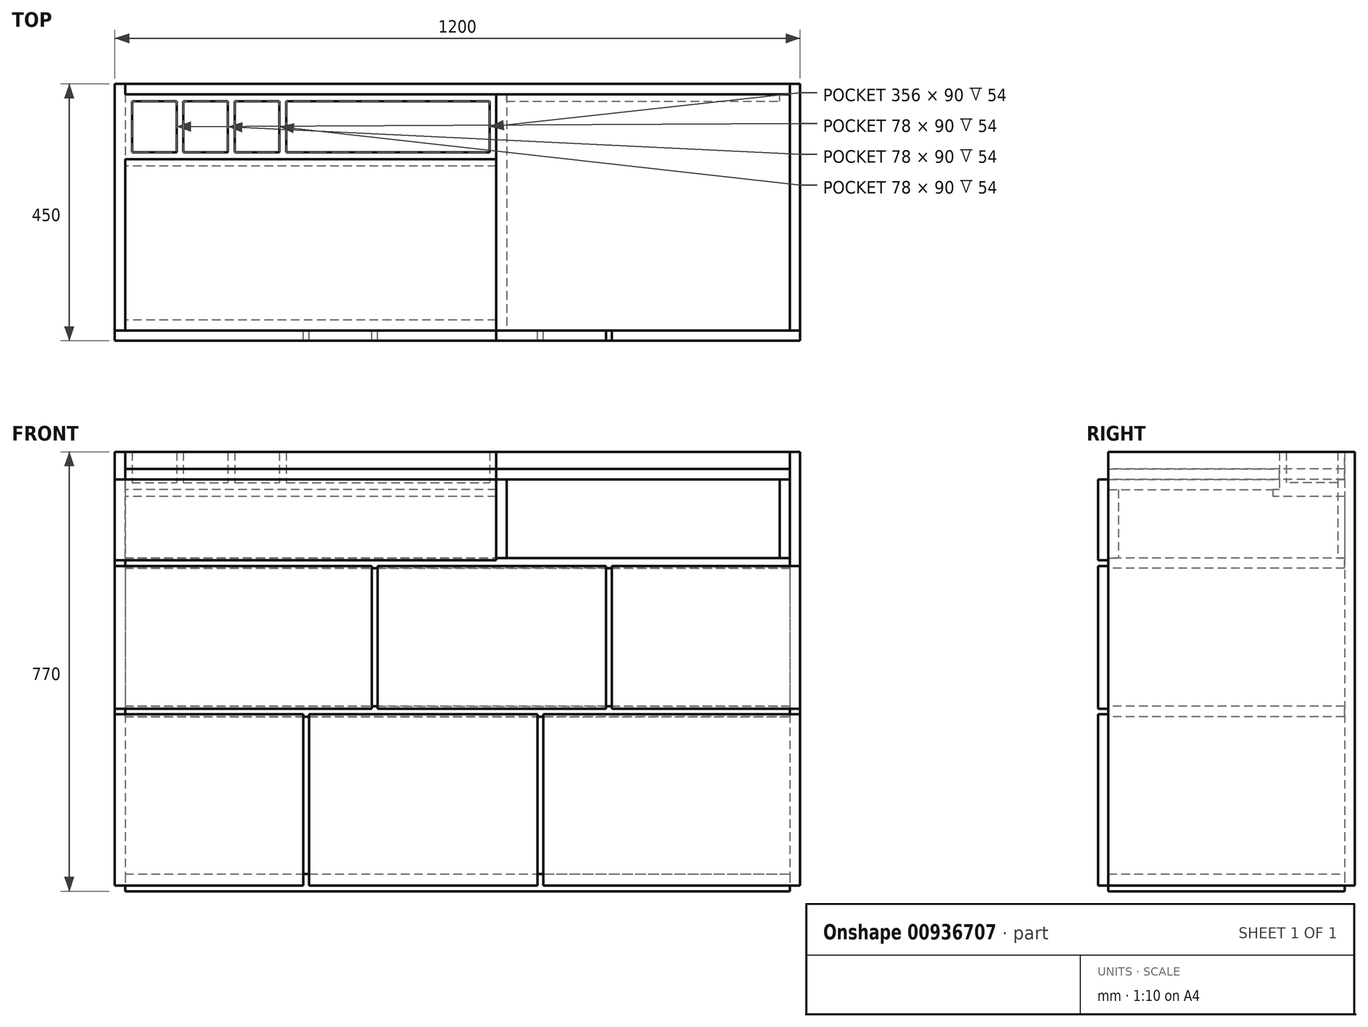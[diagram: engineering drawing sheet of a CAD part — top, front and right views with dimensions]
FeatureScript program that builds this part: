
annotation { "Feature Type Name" : "Feature", "Feature Type Description" : "" }
export const myFeature = defineFeature(function(context is Context, id is Id, definition is map)
    precondition{}
    {
        {
            var Q0;
            Q0=qCreatedBy(makeId("Top.planeOp"),FACE);
            var sketch = newSketch(context, id + "F0", { "sketchPlane" : qUnion([Q0])});
            skLineSegment(sketch, "E0.bottom", {"start": v(0, 0) * mm, "end": v(1200, 0) * mm});
            skLineSegment(sketch, "E0.top", {"start": v(0, 432) * mm, "end": v(1200, 432) * mm});
            skLineSegment(sketch, "E0.left", {"start": v(0, 0) * mm, "end": v(0, 432) * mm});
            skLineSegment(sketch, "E0.right", {"start": v(1200, 0) * mm, "end": v(1200, 432) * mm});
            skLineSegment(sketch, "E1.0", {"start": v(18, 0) * mm, "end": v(18, 432) * mm});
            skLineSegment(sketch, "E2", {"start": v(600, 455.77) * mm, "end": v(600, 504.04) * mm, "construction": true});
            skPoint(sketch, "E2.startSnap0", {"position": v(600, 432) * mm});
            skLineSegment(sketch, "E3.MirrorCS", {"start": v(1182, 0) * mm, "end": v(1182, 432) * mm});
            skLineSegment(sketch, "E4", {"start": v(1225.2, 216) * mm, "end": v(1296.23, 216) * mm, "construction": true});
            skPoint(sketch, "E4.startSnap0", {"position": v(1200, 216) * mm});
            skLineSegment(sketch, "E5.0", {"start": v(0, 414) * mm, "end": v(1200, 414) * mm});
            skSolve(sketch);
        }
        {
            var Q0;
            {var subQ0=sQuery(id+"F0.wireOp",EDGE,"E0.left");var subQ1=sQuery(id+"F0.wireOp",EDGE,"E0.bottom");var subQ2=makeQuery(id+"F0.imprint","INTERSECT",VERTEX,{"derivedFrom":[subQ1,subQ0]});Q0=makeQuery(id+"F0.imprint","IMPRINT",FACE,{"disambiguationData":[TD([[makeQuery(id+"F0.imprint","IMPRINT",EDGE,{"disambiguationData":[TD([[subQ2,-1.0]])],"derivedFrom":subQ1}),1.0]])]});}
            var Q1;
            {var subQ0=sQuery(id+"F0.wireOp",EDGE,"E0.left");var subQ1=sQuery(id+"F0.wireOp",EDGE,"E0.top");var subQ2=makeQuery(id+"F0.imprint","INTERSECT",VERTEX,{"derivedFrom":[subQ1,subQ0]});Q1=makeQuery(id+"F0.imprint","IMPRINT",FACE,{"disambiguationData":[TD([[makeQuery(id+"F0.imprint","IMPRINT",EDGE,{"disambiguationData":[TD([[subQ2,-1.0]])],"derivedFrom":subQ1}),-1.0]])]});}
            var Q2;
            {var subQ0=sQuery(id+"F0.wireOp",EDGE,"E0.right");var subQ1=sQuery(id+"F0.wireOp",EDGE,"E0.bottom");var subQ2=makeQuery(id+"F0.imprint","INTERSECT",VERTEX,{"derivedFrom":[subQ1,subQ0]});Q2=makeQuery(id+"F0.imprint","IMPRINT",FACE,{"disambiguationData":[TD([[makeQuery(id+"F0.imprint","IMPRINT",EDGE,{"disambiguationData":[TD([[subQ2,1.0]])],"derivedFrom":subQ1}),1.0]])]});}
            var Q3;
            {var subQ0=sQuery(id+"F0.wireOp",EDGE,"E0.right");var subQ1=sQuery(id+"F0.wireOp",EDGE,"E0.top");var subQ2=makeQuery(id+"F0.imprint","INTERSECT",VERTEX,{"derivedFrom":[subQ1,subQ0]});Q3=makeQuery(id+"F0.imprint","IMPRINT",FACE,{"disambiguationData":[TD([[makeQuery(id+"F0.imprint","IMPRINT",EDGE,{"disambiguationData":[TD([[subQ2,1.0]])],"derivedFrom":subQ1}),-1.0]])]});}
            extrude(context, id + "F1", {"entities" : qUnion([Q0, Q1, Q2, Q3]), "depth" : 760 * mm, "offsetDistance" : 25 * mm});
        }
        {
            var Q0;
            {var subQ0=sQuery(id+"F0.wireOp",EDGE,"E1.0");var subQ1=sQuery(id+"F0.wireOp",EDGE,"E0.top");var subQ2=makeQuery(id+"F0.imprint","INTERSECT",VERTEX,{"derivedFrom":[subQ1,subQ0]});Q0=makeQuery(id+"F0.imprint","IMPRINT",FACE,{"disambiguationData":[TD([[makeQuery(id+"F0.imprint","IMPRINT",EDGE,{"disambiguationData":[TD([[subQ2,-1.0]])],"derivedFrom":subQ1}),-1.0]])]});}
            var Q1;
            Q1=makeQuery(id+"F1.opExtrude","CAP_FACE",FACE,{"disambiguationData":[OSD([sQuery(id+"F0.wireOp",EDGE,"E0.bottom"),sQuery(id+"F0.wireOp",EDGE,"E0.top"),sQuery(id+"F0.wireOp",EDGE,"E0.left"),sQuery(id+"F0.wireOp",EDGE,"E1.0")])],"isStart":false});
            extrude(context, id + "F2", {"entities" : qUnion([Q0]), "endBound" : BoundingType.UP_TO_SURFACE, "depth" : 25 * mm, "endBoundEntityFace" : qUnion([Q1]), "offsetDistance" : 25 * mm});
        }
        {
            var Q0;
            {var subQ0=sQuery(id+"F0.wireOp",EDGE,"E1.0");var subQ1=sQuery(id+"F0.wireOp",EDGE,"E0.bottom");var subQ2=makeQuery(id+"F0.imprint","INTERSECT",VERTEX,{"derivedFrom":[subQ1,subQ0]});Q0=makeQuery(id+"F0.imprint","IMPRINT",FACE,{"disambiguationData":[TD([[makeQuery(id+"F0.imprint","IMPRINT",EDGE,{"disambiguationData":[TD([[subQ2,-1.0]])],"derivedFrom":subQ1}),1.0]])]});}
            extrude(context, id + "F3", {"entities" : qUnion([Q0]), "depth" : 20 * mm, "offsetDistance" : 25 * mm, "hasSecondDirection" : true, "secondDirectionOppositeDirection" : true, "secondDirectionDepth" : 10 * mm});
        }
        {
            var Q0;
            Q0=makeQuery(id+"F1.opExtrude","CAP_FACE",FACE,{"disambiguationData":[OSD([sQuery(id+"F0.wireOp",EDGE,"E0.bottom"),sQuery(id+"F0.wireOp",EDGE,"E0.top"),sQuery(id+"F0.wireOp",EDGE,"E0.left"),sQuery(id+"F0.wireOp",EDGE,"E1.0")])],"isStart":false});
            var sketch = newSketch(context, id + "F4", { "sketchPlane" : qUnion([Q0])});
            skLineSegment(sketch, "E6.bottom", {"start": v(0, 432) * mm, "end": v(1200, 432) * mm});
            skLineSegment(sketch, "E6.top", {"start": v(0, 0) * mm, "end": v(1200, 0) * mm});
            skLineSegment(sketch, "E6.left", {"start": v(0, 432) * mm, "end": v(0, 0) * mm});
            skLineSegment(sketch, "E6.right", {"start": v(1200, 432) * mm, "end": v(1200, 0) * mm});
            skLineSegment(sketch, "E7.bottom", {"start": v(18, 0) * mm, "end": v(1182, 0) * mm});
            skLineSegment(sketch, "E7.top", {"start": v(18, 414) * mm, "end": v(1182, 414) * mm});
            skLineSegment(sketch, "E7.left", {"start": v(18, 0) * mm, "end": v(18, 414) * mm});
            skLineSegment(sketch, "E7.right", {"start": v(1182, 0) * mm, "end": v(1182, 414) * mm});
            skLineSegment(sketch, "E8", {"start": v(668, 414) * mm, "end": v(668, 0) * mm});
            skLineSegment(sketch, "E9", {"start": v(18, 300) * mm, "end": v(668, 300) * mm});
            skLineSegment(sketch, "E10", {"start": v(55.2, 414) * mm, "end": v(55.2, -186) * mm, "construction": true});
            skLineSegment(sketch, "E11", {"start": v(-81.86, 114) * mm, "end": v(55.2, 114) * mm, "construction": true});
            skLineSegment(sketch, "E12", {"start": v(55.2, 0) * mm, "end": v(-78.13, 0) * mm, "construction": true});
            skLineSegment(sketch, "E13", {"start": v(55.2, -186) * mm, "end": v(-68.9, -186) * mm, "construction": true});
            skSolve(sketch);
        }
        {
            var Q0;
            {var subQ5=sQuery(id+"F4.wireOp",EDGE,"E9");Q0=makeQuery(id+"F4.imprint","IMPRINT",FACE,{"disambiguationData":[TD([[makeQuery(id+"F4.imprint","IMPRINT",EDGE,{"derivedFrom":subQ5}),-1.0]])]});}
            extrude(context, id + "F5", {"entities" : qUnion([Q0]), "oppositeDirection" : true, "depth" : 18 * mm, "offsetDistance" : 25 * mm});
        }
        {
            var Q0;
            {var subQ0=sQuery(id+"F4.wireOp",EDGE,"E7.right");Q0=makeQuery(id+"F4.imprint","IMPRINT",FACE,{"disambiguationData":[TD([[makeQuery(id+"F4.imprint","IMPRINT",EDGE,{"derivedFrom":subQ0}),1.0]])]});}
            extrude(context, id + "F6", {"entities" : qUnion([Q0]), "oppositeDirection" : true, "depth" : 18 * mm, "offsetDistance" : 25 * mm});
        }
        {
            var Q0;
            Q0=makeQuery(id+"F5.opExtrude","SWEPT_BODY",BODY,{"disambiguationData":[OSD([sQuery(id+"F4.wireOp",EDGE,"E7.bottom"),sQuery(id+"F4.wireOp",EDGE,"E7.top"),sQuery(id+"F4.wireOp",EDGE,"E7.left"),sQuery(id+"F4.wireOp",EDGE,"E8")])]});
            var Q1;
            Q1=makeQuery(id+"F6.opExtrude","SWEPT_BODY",BODY,{"disambiguationData":[OSD([sQuery(id+"F4.wireOp",EDGE,"E7.bottom"),sQuery(id+"F4.wireOp",EDGE,"E7.top"),sQuery(id+"F4.wireOp",EDGE,"E7.right"),sQuery(id+"F4.wireOp",EDGE,"E8")])]});
            transform(context, id + "F7", {"entities" : qUnion([Q0, Q1]), "transformType" : TransformType.TRANSLATION_3D, "dx" : 0 * mm, "dy" : 0 * mm, "dz" : -30 * mm, "makeCopy" : false});
        }
        {
            var Q0;
            {var subQ0=sQuery(id+"F0.wireOp",EDGE,"E0.bottom");Q0=makeQuery(id+"F1.opExtrude","SWEPT_FACE",FACE,{"disambiguationData":[OSD([subQ0]),TDD([makeQuery(id+"F0.imprint","IMPRINT",EDGE,{"disambiguationData":[TD([[makeQuery(id+"F0.imprint","INTERSECT",VERTEX,{"derivedFrom":[subQ0,sQuery(id+"F0.wireOp",EDGE,"E0.left")]}),-1.0]])],"derivedFrom":subQ0})])]});}
            var sketch = newSketch(context, id + "F8", { "sketchPlane" : qUnion([Q0])});
            skLineSegment(sketch, "E14.bottom", {"start": v(0, 730) * mm, "end": v(668, 730) * mm});
            skLineSegment(sketch, "E14.top", {"start": v(0, 570) * mm, "end": v(668, 570) * mm});
            skLineSegment(sketch, "E14.left", {"start": v(0, 730) * mm, "end": v(0, 570) * mm});
            skLineSegment(sketch, "E14.right", {"start": v(668, 730) * mm, "end": v(668, 570) * mm});
            skLineSegment(sketch, "E15.bottom", {"start": v(1200, 560) * mm, "end": v(870, 560) * mm});
            skLineSegment(sketch, "E15.top", {"start": v(1200, 310) * mm, "end": v(870, 310) * mm});
            skLineSegment(sketch, "E15.left", {"start": v(1200, 560) * mm, "end": v(1200, 310) * mm});
            skLineSegment(sketch, "E15.right", {"start": v(870, 560) * mm, "end": v(870, 310) * mm});
            skLineSegment(sketch, "E16.bottom", {"start": v(860, 560) * mm, "end": v(460, 560) * mm});
            skLineSegment(sketch, "E16.top", {"start": v(860, 310) * mm, "end": v(460, 310) * mm});
            skLineSegment(sketch, "E16.left", {"start": v(860, 560) * mm, "end": v(860, 310) * mm});
            skLineSegment(sketch, "E16.right", {"start": v(460, 560) * mm, "end": v(460, 310) * mm});
            skLineSegment(sketch, "E17.bottom", {"start": v(450, 560) * mm, "end": v(0, 560) * mm});
            skLineSegment(sketch, "E17.top", {"start": v(450, 310) * mm, "end": v(0, 310) * mm});
            skLineSegment(sketch, "E17.left", {"start": v(450, 560) * mm, "end": v(450, 310) * mm});
            skLineSegment(sketch, "E17.right", {"start": v(0, 560) * mm, "end": v(0, 310) * mm});
            skLineSegment(sketch, "E18.bottom", {"start": v(678, 730) * mm, "end": v(1200, 730) * mm});
            skLineSegment(sketch, "E18.top", {"start": v(678, 570) * mm, "end": v(1200, 570) * mm});
            skLineSegment(sketch, "E18.left", {"start": v(678, 730) * mm, "end": v(678, 570) * mm});
            skLineSegment(sketch, "E18.right", {"start": v(1200, 730) * mm, "end": v(1200, 570) * mm});
            skLineSegment(sketch, "E19", {"start": v(668, 650) * mm, "end": v(678, 650) * mm, "construction": true});
            skLineSegment(sketch, "E20", {"start": v(1108.22, 570) * mm, "end": v(1108.22, 560) * mm, "construction": true});
            skLineSegment(sketch, "E21", {"start": v(870, 435) * mm, "end": v(860, 435) * mm, "construction": true});
            skLineSegment(sketch, "E22", {"start": v(460, 435) * mm, "end": v(450, 435) * mm, "construction": true});
            skLineSegment(sketch, "E23.bottom", {"start": v(0, 0) * mm, "end": v(330, 0) * mm});
            skLineSegment(sketch, "E23.top", {"start": v(0, 300) * mm, "end": v(330, 300) * mm});
            skLineSegment(sketch, "E23.left", {"start": v(0, 0) * mm, "end": v(0, 300) * mm});
            skLineSegment(sketch, "E23.right", {"start": v(330, 0) * mm, "end": v(330, 300) * mm});
            skLineSegment(sketch, "E24.bottom", {"start": v(340, 300) * mm, "end": v(740, 300) * mm});
            skLineSegment(sketch, "E24.top", {"start": v(340, 0) * mm, "end": v(740, 0) * mm});
            skLineSegment(sketch, "E24.left", {"start": v(340, 300) * mm, "end": v(340, 0) * mm});
            skLineSegment(sketch, "E24.right", {"start": v(740, 300) * mm, "end": v(740, 0) * mm});
            skLineSegment(sketch, "E25.bottom", {"start": v(750, 300) * mm, "end": v(1200, 300) * mm});
            skLineSegment(sketch, "E25.top", {"start": v(750, 0) * mm, "end": v(1200, 0) * mm});
            skLineSegment(sketch, "E25.left", {"start": v(750, 300) * mm, "end": v(750, 0) * mm});
            skLineSegment(sketch, "E25.right", {"start": v(1200, 300) * mm, "end": v(1200, 0) * mm});
            skLineSegment(sketch, "E26", {"start": v(165, 310) * mm, "end": v(165, 300) * mm, "construction": true});
            skPoint(sketch, "E26.startSnap0", {"position": v(165, 300) * mm});
            skLineSegment(sketch, "E27", {"start": v(330, 150) * mm, "end": v(340, 150) * mm, "construction": true});
            skLineSegment(sketch, "E28", {"start": v(750, 150) * mm, "end": v(740, 150) * mm, "construction": true});
            skLineSegment(sketch, "E29.bottom", {"start": v(678, 570) * mm, "end": v(1182, 570) * mm});
            skLineSegment(sketch, "E29.top", {"start": v(678, 588) * mm, "end": v(1182, 588) * mm});
            skLineSegment(sketch, "E29.left", {"start": v(678, 570) * mm, "end": v(678, 588) * mm});
            skLineSegment(sketch, "E29.right", {"start": v(1182, 570) * mm, "end": v(1182, 588) * mm});
            skLineSegment(sketch, "E30", {"start": v(668, 712) * mm, "end": v(0, 712) * mm});
            skSolve(sketch);
        }
        {
            var Q0;
            {var subQ0=sQuery(id+"F8.wireOp",EDGE,"E17.left");Q0=makeQuery(id+"F8.imprint","IMPRINT",FACE,{"disambiguationData":[TD([[makeQuery(id+"F8.imprint","IMPRINT",EDGE,{"derivedFrom":subQ0}),-1.0]])]});}
            var Q1;
            Q1=makeQuery(id+"F8.imprint","IMPRINT",FACE,{"disambiguationData":[TD([[makeQuery(id+"F8.imprint","IMPRINT",EDGE,{"derivedFrom":sQuery(id+"F8.wireOp",EDGE,"E16.bottom")}),1.0]])]});
            var Q2;
            Q2=makeQuery(id+"F8.imprint","IMPRINT",FACE,{"disambiguationData":[TD([[makeQuery(id+"F8.imprint","IMPRINT",EDGE,{"derivedFrom":sQuery(id+"F8.wireOp",EDGE,"E15.bottom")}),1.0]])]});
            var Q3;
            Q3=makeQuery(id+"F8.imprint","IMPRINT",FACE,{"disambiguationData":[TD([[makeQuery(id+"F8.imprint","IMPRINT",EDGE,{"derivedFrom":sQuery(id+"F8.wireOp",EDGE,"E25.bottom")}),-1.0]])]});
            var Q4;
            Q4=makeQuery(id+"F8.imprint","IMPRINT",FACE,{"disambiguationData":[TD([[makeQuery(id+"F8.imprint","IMPRINT",EDGE,{"derivedFrom":sQuery(id+"F8.wireOp",EDGE,"E24.bottom")}),-1.0]])]});
            var Q5;
            {var subQ3=sQuery(id+"F8.wireOp",EDGE,"E23.right");Q5=makeQuery(id+"F8.imprint","IMPRINT",FACE,{"disambiguationData":[TD([[makeQuery(id+"F8.imprint","IMPRINT",EDGE,{"derivedFrom":subQ3}),1.0]])]});}
            var Q6;
            {var subQ0=sQuery(id+"F8.wireOp",EDGE,"E17.right");Q6=makeQuery(id+"F8.imprint","IMPRINT",FACE,{"disambiguationData":[TD([[makeQuery(id+"F8.imprint","IMPRINT",EDGE,{"derivedFrom":subQ0}),1.0]])]});}
            var Q7;
            {var subQ0=sQuery(id+"F8.wireOp",EDGE,"E23.left");Q7=makeQuery(id+"F8.imprint","IMPRINT",FACE,{"disambiguationData":[TD([[makeQuery(id+"F8.imprint","IMPRINT",EDGE,{"derivedFrom":subQ0}),1.0]])]});}
            var Q8;
            {var subQ0=sQuery(id+"F8.wireOp",EDGE,"E14.right");var subQ1=sQuery(id+"F8.wireOp",EDGE,"E14.top");var subQ2=makeQuery(id+"F8.imprint","INTERSECT",VERTEX,{"derivedFrom":[subQ1,subQ0]});Q8=makeQuery(id+"F8.imprint","IMPRINT",FACE,{"disambiguationData":[TD([[makeQuery(id+"F8.imprint","IMPRINT",EDGE,{"disambiguationData":[TD([[subQ2,1.0]])],"derivedFrom":subQ0}),-1.0]])]});}
            var Q9;
            {var subQ0=sQuery(id+"F8.wireOp",EDGE,"E14.left");var subQ6=sQuery(id+"F8.wireOp",EDGE,"E30");var subQ7=makeQuery(id+"F8.imprint","INTERSECT",VERTEX,{"derivedFrom":[subQ0,subQ6]});Q9=makeQuery(id+"F8.imprint","IMPRINT",FACE,{"disambiguationData":[TD([[makeQuery(id+"F8.imprint","IMPRINT",EDGE,{"disambiguationData":[TD([[subQ7,1.0]])],"derivedFrom":subQ6}),1.0]])]});}
            extrude(context, id + "F9", {"entities" : qUnion([Q0, Q1, Q2, Q3, Q4, Q5, Q6, Q7, Q8, Q9]), "depth" : 18 * mm, "offsetDistance" : 25 * mm});
        }
        {
            var Q0;
            Q0=makeQuery(id+"F9.opExtrude","CAP_FACE",FACE,{"disambiguationData":[OSD([sQuery(id+"F8.wireOp",EDGE,"E14.bottom"),sQuery(id+"F8.wireOp",EDGE,"E14.top"),sQuery(id+"F8.wireOp",EDGE,"E14.left"),sQuery(id+"F8.wireOp",EDGE,"E14.right")])],"isStart":true});
            var sketch = newSketch(context, id + "F10", { "sketchPlane" : qUnion([Q0])});
            skLineSegment(sketch, "E31.bottom", {"start": v(-18, 574) * mm, "end": v(-1182, 574) * mm});
            skLineSegment(sketch, "E31.top", {"start": v(-18, 556) * mm, "end": v(-1182, 556) * mm});
            skLineSegment(sketch, "E31.left", {"start": v(-18, 574) * mm, "end": v(-18, 556) * mm});
            skLineSegment(sketch, "E31.right", {"start": v(-1182, 574) * mm, "end": v(-1182, 556) * mm});
            skLineSegment(sketch, "E32.bottom", {"start": v(-18, 314) * mm, "end": v(-1182, 314) * mm});
            skLineSegment(sketch, "E32.top", {"start": v(-18, 296) * mm, "end": v(-1182, 296) * mm});
            skLineSegment(sketch, "E32.left", {"start": v(-18, 314) * mm, "end": v(-18, 296) * mm});
            skLineSegment(sketch, "E32.right", {"start": v(-1182, 314) * mm, "end": v(-1182, 296) * mm});
            skLineSegment(sketch, "E33", {"start": v(19.2, 570) * mm, "end": v(19.2, 560) * mm, "construction": true});
            skLineSegment(sketch, "E34", {"start": v(19.2, 565) * mm, "end": v(-39.84, 565) * mm, "construction": true});
            skPoint(sketch, "E35", {"position": v(-18, 565) * mm});
            skLineSegment(sketch, "E36", {"start": v(19.2, 310) * mm, "end": v(19.2, 300) * mm, "construction": true});
            skLineSegment(sketch, "E37", {"start": v(19.2, 305) * mm, "end": v(-39.5, 305) * mm, "construction": true});
            skPoint(sketch, "E38", {"position": v(-18, 305) * mm});
            skLineSegment(sketch, "E39.bottom", {"start": v(-874, 556) * mm, "end": v(-856, 556) * mm});
            skLineSegment(sketch, "E39.top", {"start": v(-874, 314) * mm, "end": v(-856, 314) * mm});
            skLineSegment(sketch, "E39.left", {"start": v(-874, 556) * mm, "end": v(-874, 314) * mm});
            skLineSegment(sketch, "E39.right", {"start": v(-856, 556) * mm, "end": v(-856, 314) * mm});
            skLineSegment(sketch, "E40.bottom", {"start": v(-464, 556) * mm, "end": v(-446, 556) * mm});
            skLineSegment(sketch, "E40.top", {"start": v(-464, 314) * mm, "end": v(-446, 314) * mm});
            skLineSegment(sketch, "E40.left", {"start": v(-464, 556) * mm, "end": v(-464, 314) * mm});
            skLineSegment(sketch, "E40.right", {"start": v(-446, 556) * mm, "end": v(-446, 314) * mm});
            skLineSegment(sketch, "E41.bottom", {"start": v(-754, 296) * mm, "end": v(-736, 296) * mm});
            skLineSegment(sketch, "E41.top", {"start": v(-754, 20) * mm, "end": v(-736, 20) * mm});
            skLineSegment(sketch, "E41.left", {"start": v(-754, 296) * mm, "end": v(-754, 20) * mm});
            skLineSegment(sketch, "E41.right", {"start": v(-736, 296) * mm, "end": v(-736, 20) * mm});
            skLineSegment(sketch, "E42.bottom", {"start": v(-344, 296) * mm, "end": v(-326, 296) * mm});
            skLineSegment(sketch, "E42.top", {"start": v(-344, 20) * mm, "end": v(-326, 20) * mm});
            skLineSegment(sketch, "E42.left", {"start": v(-344, 296) * mm, "end": v(-344, 20) * mm});
            skLineSegment(sketch, "E42.right", {"start": v(-326, 296) * mm, "end": v(-326, 20) * mm});
            skLineSegment(sketch, "E43", {"start": v(-870, 601.46) * mm, "end": v(-860, 601.46) * mm, "construction": true});
            skLineSegment(sketch, "E44", {"start": v(-450, 603.59) * mm, "end": v(-460, 603.59) * mm, "construction": true});
            skLineSegment(sketch, "E45", {"start": v(-330, 290.14) * mm, "end": v(-340, 290.14) * mm, "construction": true});
            skLineSegment(sketch, "E46", {"start": v(-740, 289.25) * mm, "end": v(-750, 289.25) * mm, "construction": true});
            skLineSegment(sketch, "E47", {"start": v(-745, 289.25) * mm, "end": v(-745, 277.23) * mm, "construction": true});
            skLineSegment(sketch, "E48", {"start": v(-335, 290.14) * mm, "end": v(-335, 284.57) * mm, "construction": true});
            skLineSegment(sketch, "E49", {"start": v(-455, 603.59) * mm, "end": v(-455, 592.26) * mm, "construction": true});
            skLineSegment(sketch, "E50", {"start": v(-865, 601.46) * mm, "end": v(-865, 596.96) * mm, "construction": true});
            skPoint(sketch, "E51", {"position": v(-745, 20) * mm});
            skPoint(sketch, "E52", {"position": v(-335, 20) * mm});
            skPoint(sketch, "E53", {"position": v(-865, 314) * mm});
            skPoint(sketch, "E54", {"position": v(-455, 314) * mm});
            skLineSegment(sketch, "E55.bottom", {"start": v(-686, 712) * mm, "end": v(-668, 712) * mm});
            skLineSegment(sketch, "E55.top", {"start": v(-686, 574) * mm, "end": v(-668, 574) * mm});
            skLineSegment(sketch, "E55.left", {"start": v(-686, 712) * mm, "end": v(-686, 574) * mm});
            skLineSegment(sketch, "E55.right", {"start": v(-668, 712) * mm, "end": v(-668, 574) * mm});
            skPoint(sketch, "E56", {"position": v(-677, 574) * mm});
            skLineSegment(sketch, "E57.bottom", {"start": v(-1182, 574) * mm, "end": v(-1164, 574) * mm});
            skLineSegment(sketch, "E57.top", {"start": v(-1182, 712) * mm, "end": v(-1164, 712) * mm});
            skLineSegment(sketch, "E57.left", {"start": v(-1182, 574) * mm, "end": v(-1182, 712) * mm});
            skLineSegment(sketch, "E57.right", {"start": v(-1164, 574) * mm, "end": v(-1164, 712) * mm});
            skSolve(sketch);
        }
        {
            var Q0;
            {var subQ8=sQuery(id+"F10.wireOp",EDGE,"E31.right");Q0=makeQuery(id+"F10.imprint","IMPRINT",FACE,{"disambiguationData":[TD([[makeQuery(id+"F10.imprint","IMPRINT",EDGE,{"derivedFrom":subQ8}),1.0]])]});}
            var Q1;
            {var subQ2=sQuery(id+"F10.wireOp",EDGE,"E32.left");Q1=makeQuery(id+"F10.imprint","IMPRINT",FACE,{"disambiguationData":[TD([[makeQuery(id+"F10.imprint","IMPRINT",EDGE,{"derivedFrom":subQ2}),-1.0]])]});}
            var Q2;
            {var subQ0=sQuery(id+"F10.wireOp",EDGE,"E31.left");var subQ1=sQuery(id+"F10.wireOp",EDGE,"E31.bottom");var subQ2=makeQuery(id+"F10.imprint","INTERSECT",VERTEX,{"derivedFrom":[subQ1,subQ0]});Q2=makeQuery(id+"F10.imprint","IMPRINT",FACE,{"disambiguationData":[TD([[makeQuery(id+"F10.imprint","IMPRINT",EDGE,{"disambiguationData":[TD([[subQ2,-1.0]])],"derivedFrom":subQ0}),-1.0]])]});}
            var Q3;
            Q3=makeQuery(id+"F6.opExtrude","SWEPT_FACE",FACE,{"disambiguationData":[OSD([sQuery(id+"F4.wireOp",EDGE,"E7.top")])]});
            extrude(context, id + "F11", {"entities" : qUnion([Q0, Q1, Q2]), "endBound" : BoundingType.UP_TO_SURFACE, "depth" : 25 * mm, "endBoundEntityFace" : qUnion([Q3]), "offsetDistance" : 25 * mm});
        }
        {
            var Q0;
            Q0=makeQuery(id+"F10.imprint","IMPRINT",FACE,{"disambiguationData":[TD([[makeQuery(id+"F10.imprint","IMPRINT",EDGE,{"derivedFrom":sQuery(id+"F10.wireOp",EDGE,"E55.bottom")}),-1.0]])]});
            var Q1;
            Q1=makeQuery(id+"F10.imprint","IMPRINT",FACE,{"disambiguationData":[TD([[makeQuery(id+"F10.imprint","IMPRINT",EDGE,{"derivedFrom":sQuery(id+"F10.wireOp",EDGE,"E39.bottom")}),-1.0]])]});
            var Q2;
            Q2=makeQuery(id+"F10.imprint","IMPRINT",FACE,{"disambiguationData":[TD([[makeQuery(id+"F10.imprint","IMPRINT",EDGE,{"derivedFrom":sQuery(id+"F10.wireOp",EDGE,"E40.bottom")}),-1.0]])]});
            var Q3;
            Q3=makeQuery(id+"F10.imprint","IMPRINT",FACE,{"disambiguationData":[TD([[makeQuery(id+"F10.imprint","IMPRINT",EDGE,{"derivedFrom":sQuery(id+"F10.wireOp",EDGE,"E42.bottom")}),-1.0]])]});
            var Q4;
            Q4=makeQuery(id+"F10.imprint","IMPRINT",FACE,{"disambiguationData":[TD([[makeQuery(id+"F10.imprint","IMPRINT",EDGE,{"derivedFrom":sQuery(id+"F10.wireOp",EDGE,"E41.bottom")}),-1.0]])]});
            var Q5;
            Q5=makeQuery(id+"F10.imprint","IMPRINT",FACE,{"disambiguationData":[TD([[makeQuery(id+"F10.imprint","IMPRINT",EDGE,{"derivedFrom":sQuery(id+"F10.wireOp",EDGE,"E57.bottom")}),1.0]])]});
            var Q6;
            Q6=makeQuery(id+"F3.opExtrude","SWEPT_FACE",FACE,{"disambiguationData":[OSD([sQuery(id+"F0.wireOp",EDGE,"E5.0")])]});
            extrude(context, id + "F12", {"entities" : qUnion([Q0, Q1, Q2, Q3, Q4, Q5]), "endBound" : BoundingType.UP_TO_SURFACE, "depth" : 25 * mm, "endBoundEntityFace" : qUnion([Q6]), "offsetDistance" : 25 * mm});
        }
        {
            var Q0;
            Q0=makeQuery(id+"F5.opExtrude","SWEPT_BODY",BODY,{"disambiguationData":[OSD([sQuery(id+"F4.wireOp",EDGE,"E7.bottom"),sQuery(id+"F4.wireOp",EDGE,"E7.left"),sQuery(id+"F4.wireOp",EDGE,"E8"),sQuery(id+"F4.wireOp",EDGE,"E9")])]});
            var Q1;
            Q1=makeQuery(id+"F5.opExtrude","SWEPT_EDGE",EDGE,{"disambiguationData":[OSD([sQuery(id+"F4.wireOp",EDGE,"E7.left"),sQuery(id+"F4.wireOp",EDGE,"E9")])]});
            transform(context, id + "F13", {"entities" : qUnion([Q0]), "transformType" : TransformType.TRANSLATION_ENTITY, "oppositeDirectionEntity" : true, "transformLine" : qUnion([Q1]), "makeCopy" : true});
        }
        {
            var Q0;
            Q0=makeQuery(id+"F2.opExtrude","SWEPT_FACE",FACE,{"disambiguationData":[OSD([sQuery(id+"F0.wireOp",EDGE,"E1.0")])]});
            var sketch = newSketch(context, id + "F14", { "sketchPlane" : qUnion([Q0])});
            skLineSegment(sketch, "E58.bottom", {"start": v(-288, 694) * mm, "end": v(-312, 694) * mm});
            skLineSegment(sketch, "E58.top", {"start": v(-288, 682) * mm, "end": v(-312, 682) * mm});
            skLineSegment(sketch, "E58.left", {"start": v(-288, 694) * mm, "end": v(-288, 682) * mm});
            skLineSegment(sketch, "E58.right", {"start": v(-312, 694) * mm, "end": v(-312, 682) * mm});
            skPoint(sketch, "E59", {"position": v(-300, 694) * mm});
            skLineSegment(sketch, "E60.bottom", {"start": v(-414, 694) * mm, "end": v(-402, 694) * mm});
            skLineSegment(sketch, "E60.top", {"start": v(-414, 682) * mm, "end": v(-402, 682) * mm});
            skLineSegment(sketch, "E60.left", {"start": v(-414, 694) * mm, "end": v(-414, 682) * mm});
            skLineSegment(sketch, "E60.right", {"start": v(-402, 694) * mm, "end": v(-402, 682) * mm});
            skLineSegment(sketch, "E61.bottom", {"start": v(-414, 694) * mm, "end": v(-300, 694) * mm});
            skLineSegment(sketch, "E61.top", {"start": v(-414, 760) * mm, "end": v(-300, 760) * mm});
            skLineSegment(sketch, "E61.left", {"start": v(-414, 694) * mm, "end": v(-414, 760) * mm});
            skLineSegment(sketch, "E61.right", {"start": v(-300, 694) * mm, "end": v(-300, 760) * mm});
            skLineSegment(sketch, "E62.bottom", {"start": v(-18, 682) * mm, "end": v(0, 682) * mm});
            skLineSegment(sketch, "E62.top", {"start": v(-18, 694) * mm, "end": v(0, 694) * mm});
            skLineSegment(sketch, "E62.left", {"start": v(-18, 682) * mm, "end": v(-18, 694) * mm});
            skLineSegment(sketch, "E62.right", {"start": v(0, 682) * mm, "end": v(0, 694) * mm});
            skLineSegment(sketch, "E63", {"start": v(-402, 682) * mm, "end": v(-312, 682) * mm});
            skLineSegment(sketch, "E64", {"start": v(-18, 682) * mm, "end": v(-18, 574) * mm});
            skLineSegment(sketch, "E65", {"start": v(-18, 574) * mm, "end": v(0, 574) * mm});
            skLineSegment(sketch, "E66", {"start": v(0, 574) * mm, "end": v(0, 682) * mm});
            skSolve(sketch);
        }
        {
            var Q0;
            Q0=makeQuery(id+"F14.imprint","IMPRINT",FACE,{"disambiguationData":[TD([[makeQuery(id+"F14.imprint","IMPRINT",EDGE,{"derivedFrom":sQuery(id+"F14.wireOp",EDGE,"E60.top")}),1.0]])]});
            var Q1;
            {var subQ1=sQuery(id+"F14.wireOp",EDGE,"E58.bottom");Q1=makeQuery(id+"F14.imprint","IMPRINT",FACE,{"disambiguationData":[TD([[makeQuery(id+"F14.imprint","IMPRINT",EDGE,{"derivedFrom":subQ1}),1.0]])]});}
            var Q2;
            Q2=makeQuery(id+"F14.imprint","IMPRINT",FACE,{"disambiguationData":[TD([[makeQuery(id+"F14.imprint","IMPRINT",EDGE,{"derivedFrom":sQuery(id+"F14.wireOp",EDGE,"E62.bottom")}),1.0]])]});
            var Q3;
            {var subQ0=sQuery(id+"F14.wireOp",EDGE,"E58.right");Q3=makeQuery(id+"F14.imprint","IMPRINT",FACE,{"disambiguationData":[TD([[makeQuery(id+"F14.imprint","IMPRINT",EDGE,{"derivedFrom":subQ0}),-1.0]])]});}
            var Q4;
            Q4=makeQuery(id+"F14.imprint","IMPRINT",FACE,{"disambiguationData":[TD([[makeQuery(id+"F14.imprint","IMPRINT",EDGE,{"derivedFrom":sQuery(id+"F14.wireOp",EDGE,"E62.bottom")}),-1.0]])]});
            var Q5;
            Q5=makeQuery(id+"F12.opExtrude","SWEPT_FACE",FACE,{"disambiguationData":[OSD([sQuery(id+"F10.wireOp",EDGE,"E55.right")])]});
            extrude(context, id + "F15", {"entities" : qUnion([Q0, Q1, Q2, Q3, Q4]), "endBound" : BoundingType.UP_TO_SURFACE, "oppositeDirection" : true, "depth" : 25 * mm, "endBoundEntityFace" : qUnion([Q5]), "offsetDistance" : 25 * mm});
        }
        {
            var Q0;
            Q0=makeQuery(id+"F15.opExtrude","SWEPT_FACE",FACE,{"disambiguationData":[OSD([sQuery(id+"F14.wireOp",EDGE,"E61.bottom")])]});
            var sketch = newSketch(context, id + "F16", { "sketchPlane" : qUnion([Q0])});
            skLineSegment(sketch, "E67.bottom", {"start": v(18, 402) * mm, "end": v(30, 402) * mm});
            skLineSegment(sketch, "E67.top", {"start": v(18, 312) * mm, "end": v(30, 312) * mm});
            skLineSegment(sketch, "E67.left", {"start": v(18, 402) * mm, "end": v(18, 312) * mm});
            skLineSegment(sketch, "E67.right", {"start": v(30, 402) * mm, "end": v(30, 312) * mm});
            skLineSegment(sketch, "E68.bottom", {"start": v(668, 312) * mm, "end": v(656, 312) * mm});
            skLineSegment(sketch, "E68.top", {"start": v(668, 402) * mm, "end": v(656, 402) * mm});
            skLineSegment(sketch, "E68.left", {"start": v(668, 402) * mm, "end": v(668, 312) * mm});
            skLineSegment(sketch, "E68.right", {"start": v(656, 402) * mm, "end": v(656, 312) * mm});
            skLineSegment(sketch, "E69.1.0.0", {"start": v(120, 402) * mm, "end": v(120, 312) * mm});
            skLineSegment(sketch, "E69.1.0.1", {"start": v(108, 402) * mm, "end": v(120, 402) * mm});
            skLineSegment(sketch, "E69.1.0.2", {"start": v(108, 402) * mm, "end": v(108, 312) * mm});
            skLineSegment(sketch, "E69.1.0.3", {"start": v(108, 312) * mm, "end": v(120, 312) * mm});
            skLineSegment(sketch, "E69.2.0.0", {"start": v(210, 402) * mm, "end": v(210, 312) * mm});
            skLineSegment(sketch, "E69.2.0.1", {"start": v(198, 402) * mm, "end": v(210, 402) * mm});
            skLineSegment(sketch, "E69.2.0.2", {"start": v(198, 402) * mm, "end": v(198, 312) * mm});
            skLineSegment(sketch, "E69.2.0.3", {"start": v(198, 312) * mm, "end": v(210, 312) * mm});
            skLineSegment(sketch, "E69.3.0.0", {"start": v(300, 402) * mm, "end": v(300, 312) * mm});
            skLineSegment(sketch, "E69.3.0.1", {"start": v(288, 402) * mm, "end": v(300, 402) * mm});
            skLineSegment(sketch, "E69.3.0.2", {"start": v(288, 402) * mm, "end": v(288, 312) * mm});
            skLineSegment(sketch, "E69.3.0.3", {"start": v(288, 312) * mm, "end": v(300, 312) * mm});
            skLineSegment(sketch, "E69.direction1", {"start": v(30, 312) * mm, "end": v(120, 312) * mm, "construction": true});
            skLineSegment(sketch, "E70.bottom", {"start": v(668, 414) * mm, "end": v(18, 414) * mm});
            skLineSegment(sketch, "E70.top", {"start": v(668, 402) * mm, "end": v(18, 402) * mm});
            skLineSegment(sketch, "E70.left", {"start": v(668, 414) * mm, "end": v(668, 402) * mm});
            skLineSegment(sketch, "E70.right", {"start": v(18, 414) * mm, "end": v(18, 402) * mm});
            skLineSegment(sketch, "E71.bottom", {"start": v(668, 312) * mm, "end": v(18, 312) * mm});
            skLineSegment(sketch, "E71.top", {"start": v(668, 300) * mm, "end": v(18, 300) * mm});
            skLineSegment(sketch, "E71.left", {"start": v(668, 312) * mm, "end": v(668, 300) * mm});
            skLineSegment(sketch, "E71.right", {"start": v(18, 312) * mm, "end": v(18, 300) * mm});
            skSolve(sketch);
        }
        {
            var Q0;
            Q0=makeQuery(id+"F16.imprint","IMPRINT",FACE,{"disambiguationData":[TD([[makeQuery(id+"F16.imprint","IMPRINT",EDGE,{"derivedFrom":sQuery(id+"F16.wireOp",EDGE,"E70.bottom")}),1.0]])]});
            var Q1;
            Q1=makeQuery(id+"F16.imprint","IMPRINT",FACE,{"disambiguationData":[TD([[makeQuery(id+"F16.imprint","IMPRINT",EDGE,{"derivedFrom":sQuery(id+"F16.wireOp",EDGE,"E71.top")}),-1.0]])]});
            var Q2;
            Q2=makeQuery(id+"F2.opExtrude","CAP_FACE",FACE,{"disambiguationData":[OSD([sQuery(id+"F0.wireOp",EDGE,"E0.top"),sQuery(id+"F0.wireOp",EDGE,"E1.0"),sQuery(id+"F0.wireOp",EDGE,"E3.MirrorCS"),sQuery(id+"F0.wireOp",EDGE,"E5.0")])],"isStart":false});
            extrude(context, id + "F17", {"entities" : qUnion([Q0, Q1]), "endBound" : BoundingType.UP_TO_SURFACE, "depth" : 25 * mm, "endBoundEntityFace" : qUnion([Q2]), "offsetDistance" : 25 * mm});
        }
        {
            var Q0;
            {var subQ0=sQuery(id+"F16.wireOp",EDGE,"E67.left");Q0=makeQuery(id+"F16.imprint","IMPRINT",FACE,{"disambiguationData":[TD([[makeQuery(id+"F16.imprint","IMPRINT",EDGE,{"derivedFrom":subQ0}),1.0]])]});}
            var Q1;
            {var subQ0=sQuery(id+"F16.wireOp",EDGE,"E69.1.0.0");Q1=makeQuery(id+"F16.imprint","IMPRINT",FACE,{"disambiguationData":[TD([[makeQuery(id+"F16.imprint","IMPRINT",EDGE,{"derivedFrom":subQ0}),-1.0]])]});}
            var Q2;
            {var subQ0=sQuery(id+"F16.wireOp",EDGE,"E69.2.0.0");Q2=makeQuery(id+"F16.imprint","IMPRINT",FACE,{"disambiguationData":[TD([[makeQuery(id+"F16.imprint","IMPRINT",EDGE,{"derivedFrom":subQ0}),-1.0]])]});}
            var Q3;
            {var subQ0=sQuery(id+"F16.wireOp",EDGE,"E69.3.0.0");Q3=makeQuery(id+"F16.imprint","IMPRINT",FACE,{"disambiguationData":[TD([[makeQuery(id+"F16.imprint","IMPRINT",EDGE,{"derivedFrom":subQ0}),-1.0]])]});}
            var Q4;
            {var subQ0=sQuery(id+"F16.wireOp",EDGE,"E68.left");Q4=makeQuery(id+"F16.imprint","IMPRINT",FACE,{"disambiguationData":[TD([[makeQuery(id+"F16.imprint","IMPRINT",EDGE,{"derivedFrom":subQ0}),1.0]])]});}
            var Q5;
            Q5=makeQuery(id+"F17.opExtrude","CAP_FACE",FACE,{"disambiguationData":[OSD([sQuery(id+"F16.wireOp",EDGE,"E70.bottom"),sQuery(id+"F16.wireOp",EDGE,"E70.top"),sQuery(id+"F16.wireOp",EDGE,"E70.left"),sQuery(id+"F16.wireOp",EDGE,"E70.right")])],"isStart":false});
            extrude(context, id + "F18", {"entities" : qUnion([Q0, Q1, Q2, Q3, Q4]), "endBound" : BoundingType.UP_TO_SURFACE, "depth" : 25 * mm, "endBoundEntityFace" : qUnion([Q5]), "offsetDistance" : 25 * mm});
        }
        {
            var Q0;
            {var subQ0=sQuery(id+"F16.wireOp",EDGE,"E67.left");Q0=makeQuery(id+"F16.imprint","IMPRINT",FACE,{"disambiguationData":[TD([[makeQuery(id+"F16.imprint","IMPRINT",EDGE,{"derivedFrom":subQ0}),1.0]])]});}
            var Q1;
            {var subQ0=sQuery(id+"F16.wireOp",EDGE,"E69.1.0.0");Q1=makeQuery(id+"F16.imprint","IMPRINT",FACE,{"disambiguationData":[TD([[makeQuery(id+"F16.imprint","IMPRINT",EDGE,{"derivedFrom":subQ0}),-1.0]])]});}
            var Q2;
            {var subQ0=sQuery(id+"F16.wireOp",EDGE,"E69.1.0.0");Q2=makeQuery(id+"F16.imprint","IMPRINT",FACE,{"disambiguationData":[TD([[makeQuery(id+"F16.imprint","IMPRINT",EDGE,{"derivedFrom":subQ0}),1.0]])]});}
            var Q3;
            {var subQ0=sQuery(id+"F16.wireOp",EDGE,"E69.2.0.0");Q3=makeQuery(id+"F16.imprint","IMPRINT",FACE,{"disambiguationData":[TD([[makeQuery(id+"F16.imprint","IMPRINT",EDGE,{"derivedFrom":subQ0}),-1.0]])]});}
            var Q4;
            {var subQ0=sQuery(id+"F16.wireOp",EDGE,"E69.2.0.0");Q4=makeQuery(id+"F16.imprint","IMPRINT",FACE,{"disambiguationData":[TD([[makeQuery(id+"F16.imprint","IMPRINT",EDGE,{"derivedFrom":subQ0}),1.0]])]});}
            var Q5;
            {var subQ0=sQuery(id+"F16.wireOp",EDGE,"E69.3.0.0");Q5=makeQuery(id+"F16.imprint","IMPRINT",FACE,{"disambiguationData":[TD([[makeQuery(id+"F16.imprint","IMPRINT",EDGE,{"derivedFrom":subQ0}),-1.0]])]});}
            var Q6;
            {var subQ0=sQuery(id+"F16.wireOp",EDGE,"E68.right");Q6=makeQuery(id+"F16.imprint","IMPRINT",FACE,{"disambiguationData":[TD([[makeQuery(id+"F16.imprint","IMPRINT",EDGE,{"derivedFrom":subQ0}),-1.0]])]});}
            var Q7;
            {var subQ0=sQuery(id+"F16.wireOp",EDGE,"E68.left");Q7=makeQuery(id+"F16.imprint","IMPRINT",FACE,{"disambiguationData":[TD([[makeQuery(id+"F16.imprint","IMPRINT",EDGE,{"derivedFrom":subQ0}),1.0]])]});}
            var Q8;
            {var subQ0=sQuery(id+"F16.wireOp",EDGE,"E67.right");Q8=makeQuery(id+"F16.imprint","IMPRINT",FACE,{"disambiguationData":[TD([[makeQuery(id+"F16.imprint","IMPRINT",EDGE,{"derivedFrom":subQ0}),1.0]])]});}
            extrude(context, id + "F19", {"entities" : qUnion([Q0, Q1, Q2, Q3, Q4, Q5, Q6, Q7, Q8]), "operationType" : NewBodyOperationType.ADD, "depth" : 12 * mm, "offsetDistance" : 25 * mm});
        }
        {
            var Q0;
            Q0=makeQuery(id+"F2.opExtrude","SWEPT_FACE",FACE,{"disambiguationData":[OSD([sQuery(id+"F0.wireOp",EDGE,"E5.0")])]});
            var sketch = newSketch(context, id + "F20", { "sketchPlane" : qUnion([Q0])});
            skLineSegment(sketch, "E72.bottom", {"start": v(686, 712) * mm, "end": v(1164, 712) * mm});
            skLineSegment(sketch, "E72.top", {"start": v(686, 574) * mm, "end": v(1164, 574) * mm});
            skLineSegment(sketch, "E72.left", {"start": v(686, 712) * mm, "end": v(686, 574) * mm});
            skLineSegment(sketch, "E72.right", {"start": v(1164, 712) * mm, "end": v(1164, 574) * mm});
            skSolve(sketch);
        }
        {
            var Q0;
            Q0=makeQuery(id+"F20.imprint","IMPRINT",FACE,{"disambiguationData":[TD([[makeQuery(id+"F20.imprint","IMPRINT",EDGE,{"derivedFrom":sQuery(id+"F20.wireOp",EDGE,"E72.bottom")}),-1.0]])]});
            extrude(context, id + "F21", {"entities" : qUnion([Q0]), "depth" : 12 * mm, "offsetDistance" : 25 * mm});
        }
    });
